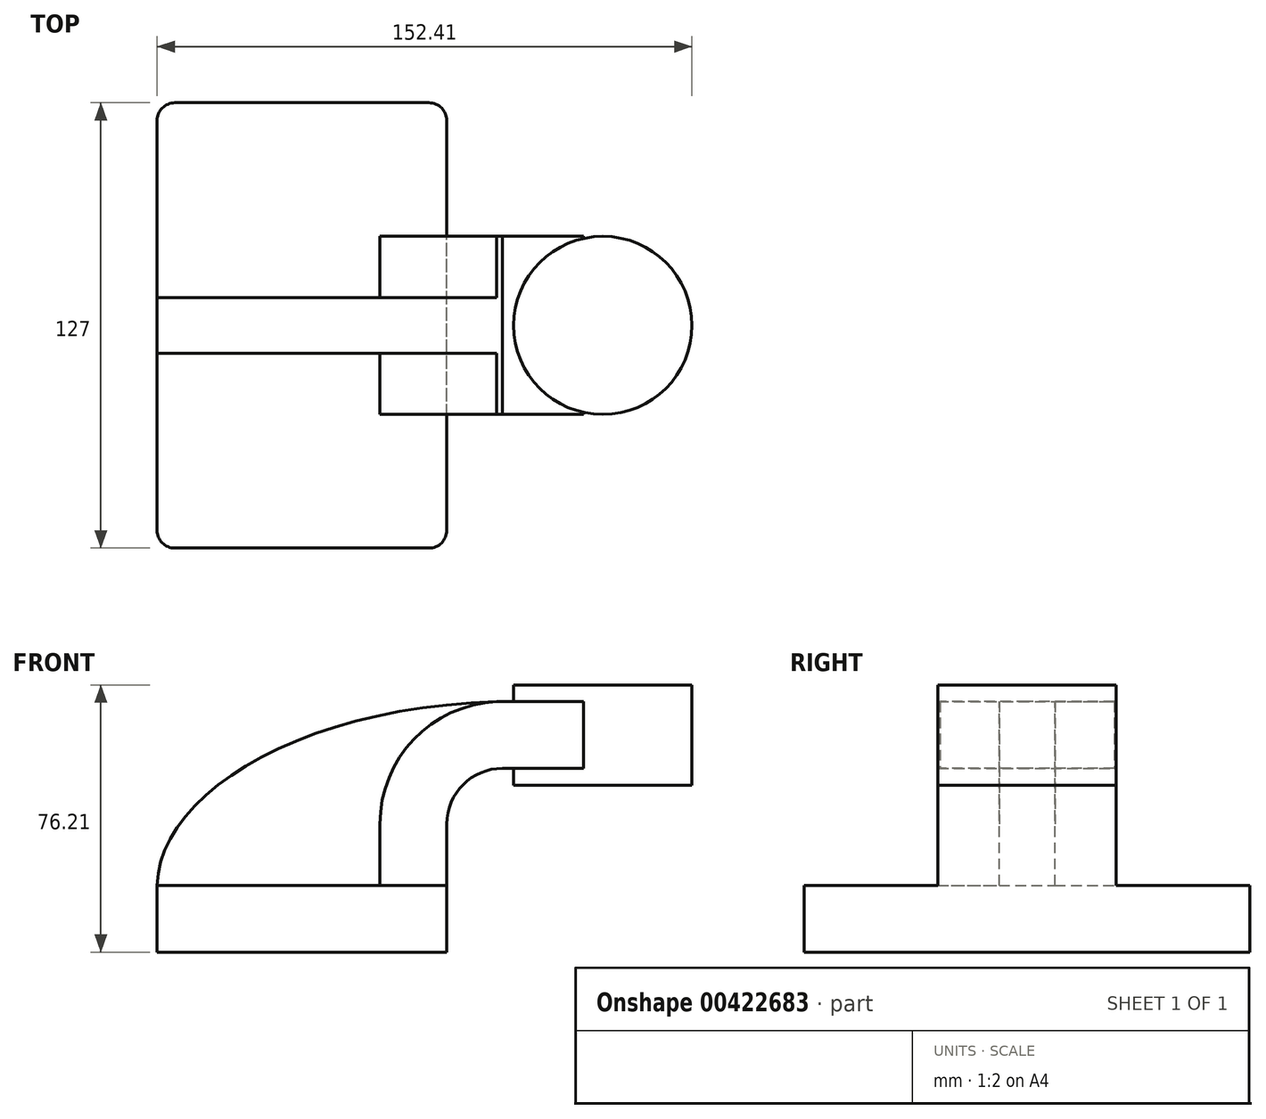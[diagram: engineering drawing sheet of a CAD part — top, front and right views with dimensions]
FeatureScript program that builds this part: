
annotation { "Feature Type Name" : "Feature", "Feature Type Description" : "" }
export const myFeature = defineFeature(function(context is Context, id is Id, definition is map)
    precondition{}
    {
        {
            var Q0;
            Q0=qCreatedBy(makeId("Front.planeOp"),FACE);
            var sketch = newSketch(context, id + "F0", { "sketchPlane" : qUnion([Q0])});
            skLineSegment(sketch, "E0.bottom", {"start": v(-41.28, 9.52) * mm, "end": v(41.27, 9.53) * mm});
            skLineSegment(sketch, "E0.top", {"start": v(-41.28, -9.53) * mm, "end": v(41.28, -9.53) * mm});
            skLineSegment(sketch, "E0.left", {"start": v(-41.28, 9.52) * mm, "end": v(-41.28, -9.53) * mm});
            skLineSegment(sketch, "E0.right", {"start": v(41.27, 9.53) * mm, "end": v(41.28, -9.52) * mm});
            skPoint(sketch, "E0.middle", {"position": v(0, 0) * mm});
            skLineSegment(sketch, "E1.bottom", {"start": v(111.12, 38.1) * mm, "end": v(60.32, 38.1) * mm});
            skLineSegment(sketch, "E1.top", {"start": v(111.12, 66.68) * mm, "end": v(60.32, 66.68) * mm});
            skLineSegment(sketch, "E1.left", {"start": v(111.12, 38.1) * mm, "end": v(111.12, 66.68) * mm});
            skLineSegment(sketch, "E1.right", {"start": v(60.32, 38.1) * mm, "end": v(60.32, 66.68) * mm});
            skPoint(sketch, "E1.middle", {"position": v(85.72, 52.39) * mm});
            skLineSegment(sketch, "E2", {"start": v(41.27, 9.53) * mm, "end": v(41.27, 27) * mm});
            skArc(sketch, "E3", {"start": v(41.27, 27) * mm, "mid": v(45.92, 38.23) * mm, "end": v(57.15, 42.88) * mm});
            skLineSegment(sketch, "E4", {"start": v(57.15, 42.88) * mm, "end": v(80.26, 42.88) * mm});
            skLineSegment(sketch, "E5.0", {"start": v(57.15, 61.93) * mm, "end": v(80.26, 61.93) * mm});
            skArc(sketch, "E5.1", {"start": v(22.22, 27) * mm, "mid": v(32.45, 51.7) * mm, "end": v(57.15, 61.93) * mm});
            skLineSegment(sketch, "E5.2", {"start": v(22.22, 9.53) * mm, "end": v(22.22, 27) * mm});
            skFitSpline(sketch, "E6", {"points": [v(-41.28, 9.52) * mm, v(57.15, 61.93) * mm], "startDerivative": vector(1.5, 78.43) * mm, "endDerivative": vector(171.45, 3.35) * mm});
            skLineSegment(sketch, "E7", {"start": v(80.26, 61.93) * mm, "end": v(80.26, 42.88) * mm});
            skLineSegment(sketch, "E8", {"start": v(85.72, 38.1) * mm, "end": v(85.72, 66.68) * mm});
            skSolve(sketch);
        }
        {
            var Q0;
            Q0=makeQuery(id+"F0.imprint","IMPRINT",FACE,{"disambiguationData":[TD([[makeQuery(id+"F0.imprint","IMPRINT",EDGE,{"derivedFrom":sQuery(id+"F0.wireOp",EDGE,"E0.top")}),1.0]])]});
            extrude(context, id + "F1", {"entities" : qUnion([Q0]), "depth" : 127 * mm, "symmetric" : true});
        }
        {
            var Q0;
            {var subQ1=sQuery(id+"F0.wireOp",EDGE,"E2");Q0=makeQuery(id+"F0.imprint","IMPRINT",FACE,{"disambiguationData":[TD([[makeQuery(id+"F0.imprint","IMPRINT",EDGE,{"derivedFrom":subQ1}),1.0]])]});}
            var Q1;
            {var subQ5=sQuery(id+"F0.wireOp",EDGE,"E7");Q1=makeQuery(id+"F0.imprint","IMPRINT",FACE,{"disambiguationData":[TD([[makeQuery(id+"F0.imprint","IMPRINT",EDGE,{"derivedFrom":subQ5}),-1.0]])]});}
            extrude(context, id + "F2", {"entities" : qUnion([Q0, Q1]), "operationType" : NewBodyOperationType.ADD, "depth" : 50.8 * mm, "symmetric" : true});
        }
        {
            var Q0;
            {var subQ3=sQuery(id+"F0.wireOp",EDGE,"E5.2");Q0=makeQuery(id+"F0.imprint","IMPRINT",FACE,{"disambiguationData":[TD([[makeQuery(id+"F0.imprint","IMPRINT",EDGE,{"derivedFrom":subQ3}),1.0]])]});}
            extrude(context, id + "F3", {"entities" : qUnion([Q0]), "operationType" : NewBodyOperationType.ADD, "depth" : 15.88 * mm, "symmetric" : true});
        }
        {
            var Q0;
            {var subQ0=sQuery(id+"F0.wireOp",EDGE,"E1.left");Q0=makeQuery(id+"F0.imprint","IMPRINT",FACE,{"disambiguationData":[TD([[makeQuery(id+"F0.imprint","IMPRINT",EDGE,{"derivedFrom":subQ0}),1.0]])]});}
            var Q1;
            Q1=sQuery(id+"F0.wireOp",EDGE,"E8");
            revolve(context, id + "F4", {"operationType" : NewBodyOperationType.ADD, "entities" : qUnion([Q0]), "axis" : qUnion([Q1]), "revolveType" : RevolveType.FULL});
        }
        {
            var Q0;
            Q0=makeQuery(id+"F1.opExtrude","CAP_EDGE",EDGE,{"disambiguationData":[OSD([sQuery(id+"F0.wireOp",EDGE,"E0.left")])],"isStart":false});
            var Q1;
            Q1=makeQuery(id+"F1.opExtrude","CAP_EDGE",EDGE,{"disambiguationData":[OSD([sQuery(id+"F0.wireOp",EDGE,"E0.right")])],"isStart":false});
            var Q2;
            Q2=makeQuery(id+"F1.opExtrude","CAP_EDGE",EDGE,{"disambiguationData":[OSD([sQuery(id+"F0.wireOp",EDGE,"E0.right")])],"isStart":true});
            var Q3;
            Q3=makeQuery(id+"F1.opExtrude","CAP_EDGE",EDGE,{"disambiguationData":[OSD([sQuery(id+"F0.wireOp",EDGE,"E0.left")])],"isStart":true});
            fillet(context, id + "F5", {"entities" : qUnion([Q0, Q1, Q2, Q3]), "radius" : 5.08 * mm, "tangentPropagation" : true, "allowEdgeOverflow" : false});
        }
    });
